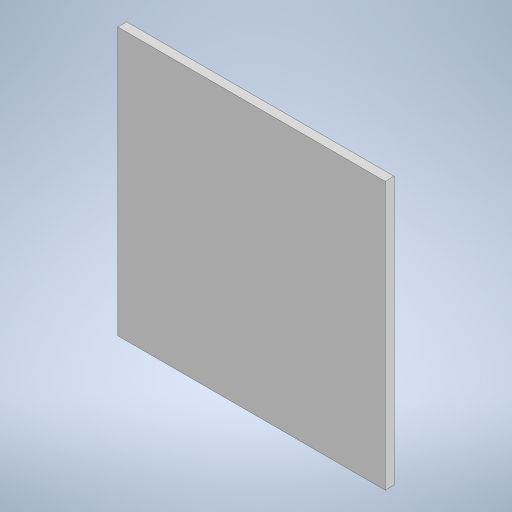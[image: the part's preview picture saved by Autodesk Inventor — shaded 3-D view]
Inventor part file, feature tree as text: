
AUTODESK INVENTOR PART (.ipt)
format: ipt  version: 2024 (Build 280153000, 153)  size: 245,760 bytes
history: native  units: mm
features: extrude x1, sketch x1
ambient origin geometry x8: Origin, YZ Plane, XZ Plane, XY Plane, X Axis, Y Axis, Z Axis, Center Point
bodies: Solid1 (feature_tree)
feature tree (2):
  extrude  "Extrusion1"  Depth=300.0mm
  sketch  "Sketch1"  dims[d0=300.0mm d1=300.0mm d2=150.0mm d3=150.0mm d4=10.0mm d5=0.0mm]
